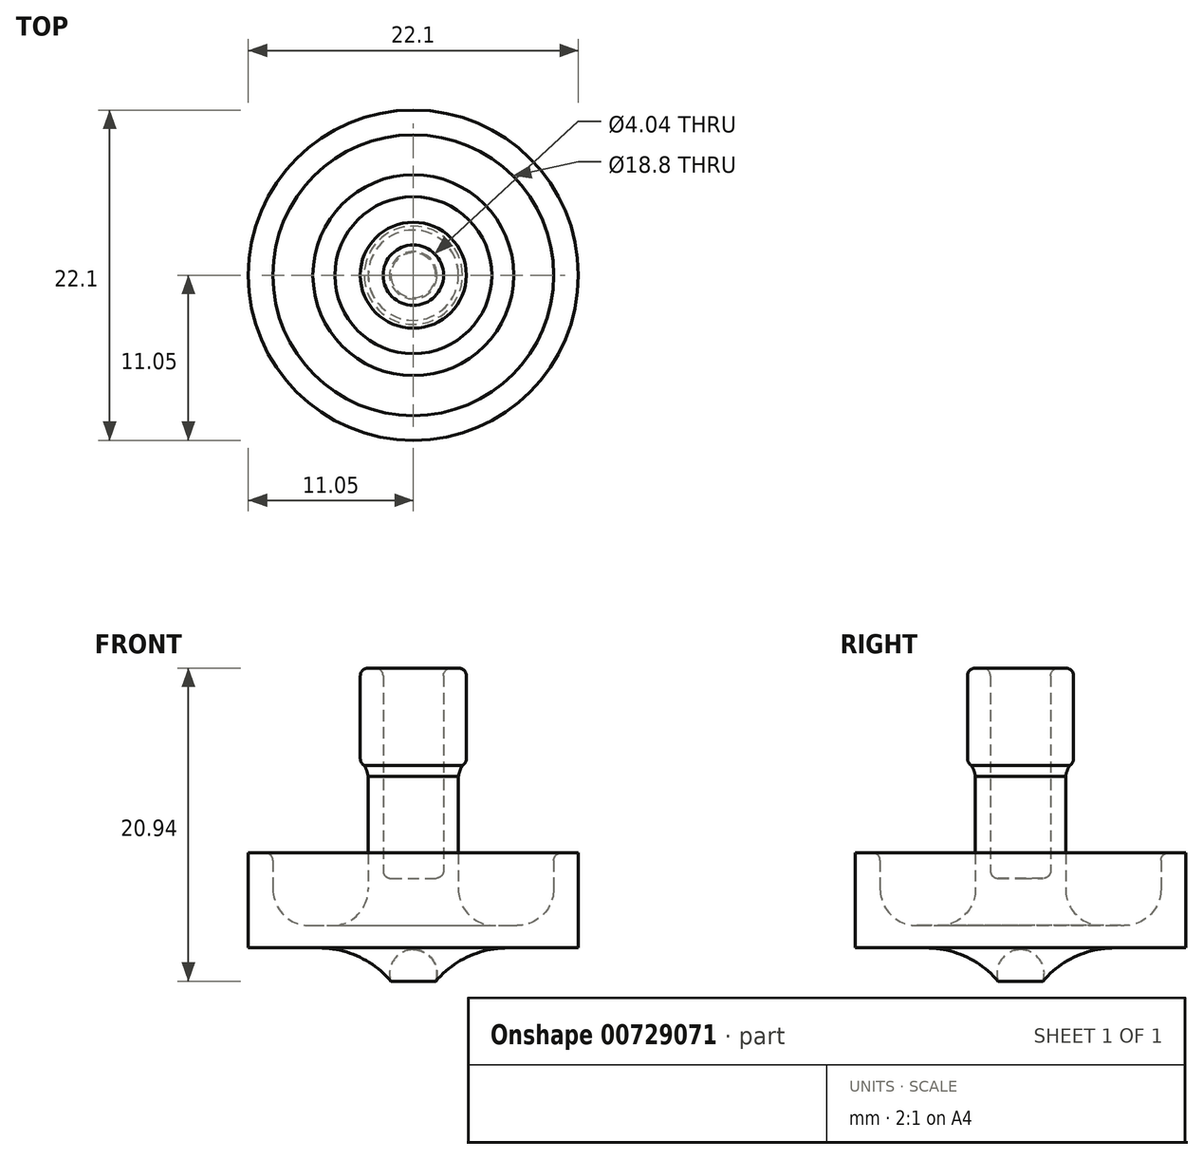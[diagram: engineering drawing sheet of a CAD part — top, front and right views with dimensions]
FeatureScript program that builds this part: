
annotation { "Feature Type Name" : "Feature", "Feature Type Description" : "" }
export const myFeature = defineFeature(function(context is Context, id is Id, definition is map)
    precondition{}
    {
        {
            var Q0;
            Q0=qCreatedBy(makeId("Front.planeOp"),FACE);
            var sketch = newSketch(context, id + "F0", { "sketchPlane" : qUnion([Q0])});
            skLineSegment(sketch, "E0.bottom", {"start": v(-6.35, 0) * mm, "end": v(-11.05, 0) * mm});
            skLineSegment(sketch, "E0.left", {"start": v(0, 0) * mm, "end": v(0, 6.35) * mm});
            skLineSegment(sketch, "E1", {"start": v(-9.4, 5.85) * mm, "end": v(-9.4, 3.93) * mm});
            skPoint(sketch, "E2.orphan", {"position": v(-12.7, 1.5) * mm});
            skPoint(sketch, "E3.end.orphan", {"position": v(-6.35, 0) * mm});
            skPoint(sketch, "E3.start.orphan", {"position": v(-6.35, 1.5) * mm});
            skLineSegment(sketch, "E4.trimOffspring", {"start": v(-9.9, 6.35) * mm, "end": v(-11.05, 6.35) * mm});
            skPoint(sketch, "E5.orphan", {"position": v(0, 1.5) * mm});
            skArc(sketch, "E6", {"start": v(-9.4, 3.93) * mm, "mid": v(-8.6, 2.13) * mm, "end": v(-6.72, 1.5) * mm});
            skPoint(sketch, "E7.orphan", {"position": v(-4.05, 1.5) * mm});
            skPoint(sketch, "E8.orphan", {"position": v(-9.4, 1.5) * mm});
            skLineSegment(sketch, "E9.top", {"start": v(0, 4.66) * mm, "end": v(-1.52, 4.66) * mm});
            skLineSegment(sketch, "E9.left", {"start": v(0, 6.35) * mm, "end": v(0, 4.66) * mm});
            skLineSegment(sketch, "E9.right", {"start": v(-2.02, 18.71) * mm, "end": v(-2.02, 5.16) * mm});
            skPoint(sketch, "E10.visualSharp", {"position": v(-12.7, 0) * mm});
            skPoint(sketch, "E11.visualSharp", {"position": v(-4.05, 20) * mm});
            skPoint(sketch, "E12.visualSharp", {"position": v(-12.7, 6.35) * mm});
            skPoint(sketch, "E13.visualSharp", {"position": v(-9.4, 6.35) * mm});
            skArc(sketch, "E13.filletArc", {"start": v(-9.4, 5.85) * mm, "mid": v(-9.55, 6.2) * mm, "end": v(-9.9, 6.35) * mm});
            skPoint(sketch, "E14.visualSharp", {"position": v(-2.02, 4.66) * mm});
            skArc(sketch, "E14.filletArc", {"start": v(-2.02, 5.16) * mm, "mid": v(-1.87, 4.8) * mm, "end": v(-1.52, 4.66) * mm});
            skArc(sketch, "E15", {"start": v(0, -0.12) * mm, "mid": v(-1.3, -0.8) * mm, "end": v(-1.5, -2.23) * mm});
            skLineSegment(sketch, "E16", {"start": v(0, 0) * mm, "end": v(0, -0.12) * mm});
            skArc(sketch, "E17", {"start": v(-1.5, -2.23) * mm, "mid": v(-3.68, -0.58) * mm, "end": v(-6.35, 0) * mm});
            skLineSegment(sketch, "E18.right", {"start": v(-4.5, 19.53) * mm, "end": v(-4.5, 19.51) * mm});
            skPoint(sketch, "E19.start.orphan", {"position": v(-4.05, 13.45) * mm});
            skArc(sketch, "E20", {"start": v(-4.5, 19.53) * mm, "mid": v(-4.5, 19.52) * mm, "end": v(-4.5, 19.51) * mm});
            skPoint(sketch, "E21.end.orphan", {"position": v(-4.05, 3.93) * mm});
            skPoint(sketch, "E22.end.orphan", {"position": v(-4.05, 6.35) * mm});
            skPoint(sketch, "E23.end.orphan", {"position": v(-4.5, 13.45) * mm});
            skLineSegment(sketch, "E24", {"start": v(-3.02, 9.9) * mm, "end": v(-3.02, 3.93) * mm});
            skLineSegment(sketch, "E25", {"start": v(-2.02, 18.71) * mm, "end": v(-3.03, 18.71) * mm});
            skArc(sketch, "E26", {"start": v(-5.25, 1.5) * mm, "mid": v(-3.66, 2.28) * mm, "end": v(-3.02, 3.93) * mm});
            skLineSegment(sketch, "E27", {"start": v(-6.72, 1.5) * mm, "end": v(-5.25, 1.5) * mm});
            skLineSegment(sketch, "E28.bottom", {"start": v(-3.03, 18.71) * mm, "end": v(-3.55, 18.71) * mm});
            skLineSegment(sketch, "E28.top", {"start": v(-3.29, 12.21) * mm, "end": v(-3.55, 12.21) * mm});
            skLineSegment(sketch, "E28.right", {"start": v(-3.55, 18.71) * mm, "end": v(-3.55, 12.21) * mm});
            skLineSegment(sketch, "E29", {"start": v(-3.02, 11.49) * mm, "end": v(-3.02, 9.9) * mm});
            skArc(sketch, "E30", {"start": v(-3.02, 11.49) * mm, "mid": v(-3.13, 11.86) * mm, "end": v(-3.29, 12.21) * mm});
            skPoint(sketch, "E31.orphan", {"position": v(-3.03, 12.21) * mm});
            skLineSegment(sketch, "E32", {"start": v(-11.05, 6.35) * mm, "end": v(-11.05, 0) * mm});
            skPoint(sketch, "E12.filletArc.start.orphan", {"position": v(-12.2, 6.35) * mm});
            skSolve(sketch);
        }
        {
            var Q0;
            Q0=makeQuery(id+"F0.imprint","IMPRINT",FACE,{"disambiguationData":[TD([[makeQuery(id+"F0.imprint","IMPRINT",EDGE,{"derivedFrom":sQuery(id+"F0.wireOp",EDGE,"E0.bottom")}),-1.0]])]});
            var Q1;
            {var subQ1=sQuery(id+"F0.wireOp",EDGE,"ff6280aa-fd3c-4f03-93f3-c40663dc82ce.top");Q1=makeQuery(id+"F0.imprint","IMPRINT",FACE,{"disambiguationData":[TD([[makeQuery(id+"F0.imprint","IMPRINT",EDGE,{"derivedFrom":subQ1}),1.0]])]});}
            var Q2;
            Q2=sQuery(id+"F0.wireOp",EDGE,"E0.left");
            revolve(context, id + "F1", {"surfaceOperationType" : NewSurfaceOperationType.NEW, "entities" : qUnion([Q0, Q1]), "axis" : qUnion([Q2]), "revolveType" : RevolveType.FULL});
        }
        {
            var Q0;
            Q0=makeQuery(id+"F1.opRevolve","SWEPT_EDGE",EDGE,{"disambiguationData":[OSD([sQuery(id+"F0.wireOp",EDGE,"E28.bottom"),sQuery(id+"F0.wireOp",EDGE,"E28.right")])]});
            var Q1;
            Q1=makeQuery(id+"F1.opRevolve","SWEPT_EDGE",EDGE,{"disambiguationData":[OSD([sQuery(id+"F0.wireOp",EDGE,"E28.top"),sQuery(id+"F0.wireOp",EDGE,"E28.right")])]});
            fillet(context, id + "F2", {"entities" : qUnion([Q0, Q1]), "radius" : .5 * mm, "tangentPropagation" : true, "allowEdgeOverflow" : false});
        }
        {
            var Q0;
            Q0=makeQuery(id+"F1.opRevolve","SWEPT_EDGE",EDGE,{"disambiguationData":[OSD([sQuery(id+"F0.wireOp",EDGE,"E9.right"),sQuery(id+"F0.wireOp",EDGE,"E25")])]});
            fillet(context, id + "F3", {"entities" : qUnion([Q0]), "radius" : .5 * mm, "tangentPropagation" : true, "allowEdgeOverflow" : false});
        }
    });
